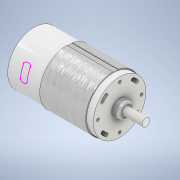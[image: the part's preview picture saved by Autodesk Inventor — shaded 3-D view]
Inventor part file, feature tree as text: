
AUTODESK INVENTOR PART (.ipt)
format: ipt  version: 2020 (Build 240168000, 168)  size: 228,864 bytes
history: native  units: in
note: dims shown in document units (in); Inventor stores cm internally (conversion verified against a paired STEP export)
features: sketch x9, extrude x8, fillet x1, other x1
ambient origin geometry x8: Origin, YZ Plane, XZ Plane, XY Plane, X Axis, Y Axis, Z Axis, Center Point
bodies: Solid1 (feature_tree)
feature tree (19):
  extrude  "Extrusion1"  Depth=2.5591in TaperAngle=0.0deg
  extrude  "Extrusion2"  Depth=0.2362in
  fillet  "Fillet1"  Radius=0.1969in
  extrude  "Extrusion3"  Depth=1.5748in TaperAngle=0.0deg
  extrude  "Extrusion4"  Depth=0.1575in
  extrude  "Extrusion5"  Depth=1.5748in TaperAngle=360.0deg
  extrude  "Extrusion6"  Depth=0.3937in TaperAngle=0.0deg
  sketch  "3D Sketch1"
  extrude  "Extrusion7"  Depth=0.7874in TaperAngle=0.0deg
  extrude  "Extrusion8"  Depth=0.0344in
  sketch  "Sketch1"  dims[d0=1.5748in d1=2.5591in d2=0.0in]
  sketch  "Sketch2"  dims[d3=0.4724in d4=0.2362in d5=0.1969in d6=0.0in]
  sketch  "Sketch3"  dims[d7=0.0787in d8=1.5748in d9=0.0in]
  sketch  "Sketch4"  dims[d10=0.1969in d11=0.0in d12=0.1575in]
  sketch  "Sketch5"  dims[d13=0.0in d14=0.0in d15=1.5748in d17=360.0deg]
  sketch  "Sketch6"  dims[d19=1.5748in d21=360.0deg d23=0.3937in d24=0.0in]
  other  "Project to Surface1"
  sketch  "Sketch8"  dims[d28=0.0787in d29=0.0in d30=0.7874in d31=0.0in]
  sketch  "Sketch9"  dims[d32=0.0197in d33=0.0344in]
